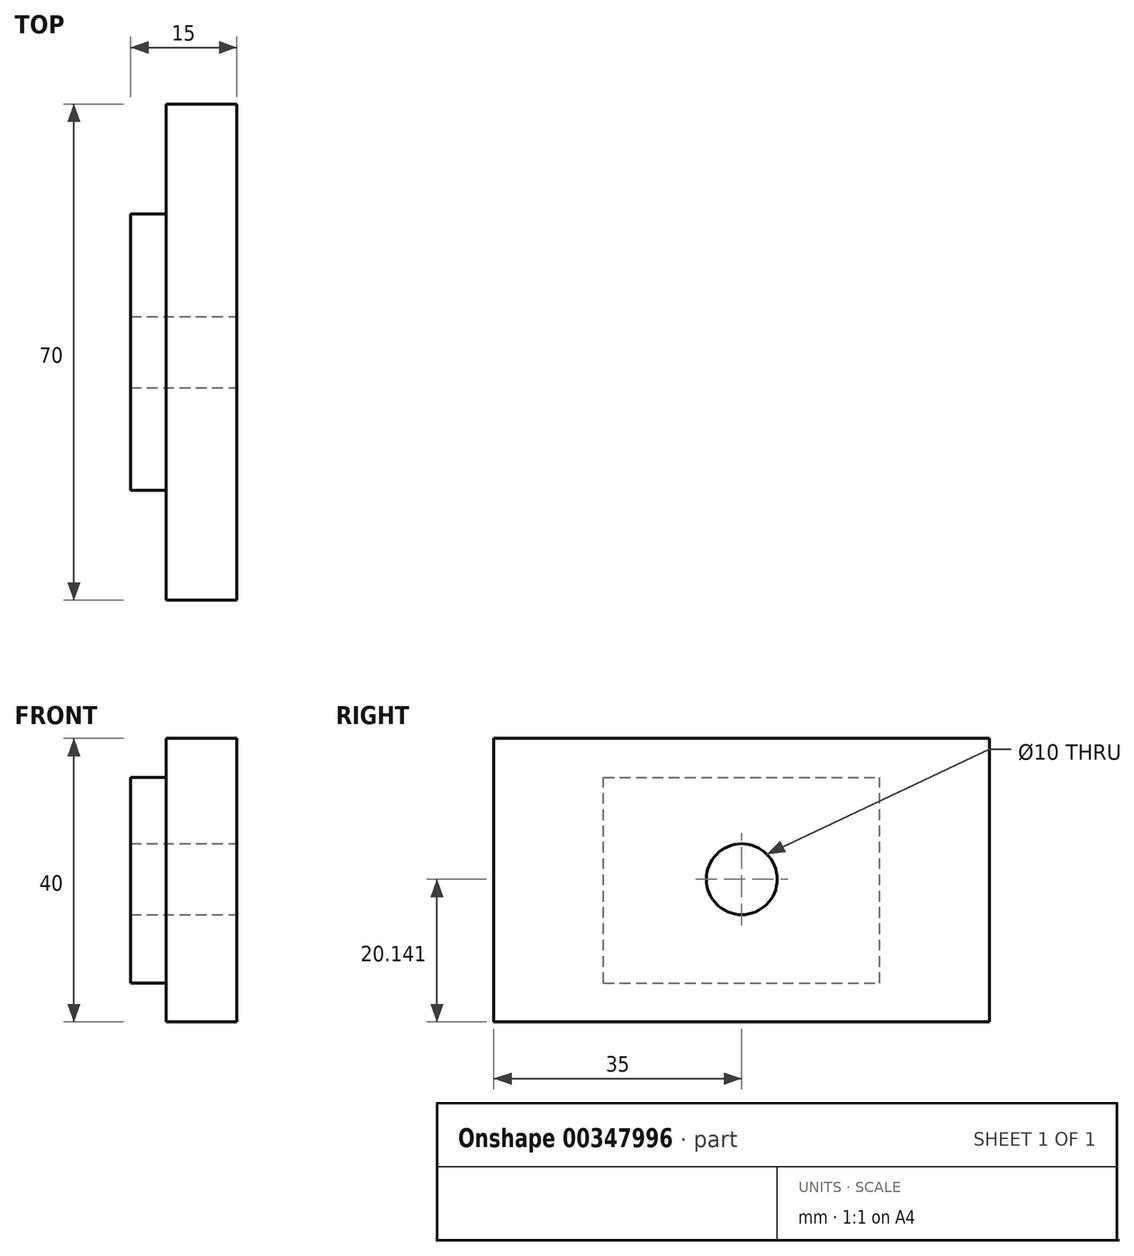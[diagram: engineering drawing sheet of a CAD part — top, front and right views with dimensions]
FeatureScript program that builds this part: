
annotation { "Feature Type Name" : "Feature", "Feature Type Description" : "" }
export const myFeature = defineFeature(function(context is Context, id is Id, definition is map)
    precondition{}
    {
        {
            var Q0;
            Q0=qCreatedBy(makeId("Right.planeOp"),FACE);
            var sketch = newSketch(context, id + "F0", { "sketchPlane" : qUnion([Q0])});
            skLineSegment(sketch, "E0.bottom", {"start": v(0, 0) * mm, "end": v(70, 0) * mm});
            skLineSegment(sketch, "E0.top", {"start": v(0, 40) * mm, "end": v(70, 40) * mm});
            skLineSegment(sketch, "E0.left", {"start": v(0, 0) * mm, "end": v(0, 40) * mm});
            skLineSegment(sketch, "E0.right", {"start": v(70, 0) * mm, "end": v(70, 40) * mm});
            skSolve(sketch);
        }
        {
            var Q0;
            Q0=qSketchRegion(id+"F0",true);
            extrude(context, id + "F1", {"entities" : qUnion([Q0]), "depth" : 10 * mm});
        }
        {
            var Q0;
            Q0=makeQuery(id+"F1.opExtrude","CAP_FACE",FACE,{"disambiguationData":[OSD([sQuery(id+"F0.wireOp",EDGE,"E0.bottom"),sQuery(id+"F0.wireOp",EDGE,"E0.top"),sQuery(id+"F0.wireOp",EDGE,"E0.left"),sQuery(id+"F0.wireOp",EDGE,"E0.right")])],"isStart":false});
            var sketch = newSketch(context, id + "F2", { "sketchPlane" : qUnion([Q0])});
            skLineSegment(sketch, "E1.bottom", {"start": v(15.5, 5.5) * mm, "end": v(54.5, 5.5) * mm});
            skLineSegment(sketch, "E1.top", {"start": v(15.5, 34.5) * mm, "end": v(54.5, 34.5) * mm});
            skLineSegment(sketch, "E1.left", {"start": v(15.5, 5.5) * mm, "end": v(15.5, 34.5) * mm});
            skLineSegment(sketch, "E1.right", {"start": v(54.5, 5.5) * mm, "end": v(54.5, 34.5) * mm});
            skSolve(sketch);
        }
        {
            var Q0;
            Q0=qSketchRegion(id+"F2",true);
            extrude(context, id + "F3", {"entities" : qUnion([Q0]), "operationType" : NewBodyOperationType.ADD, "oppositeDirection" : true, "depth" : 15 * mm});
        }
        {
            var Q0;
            Q0=makeQuery(id+"F1.opExtrude","CAP_FACE",FACE,{"disambiguationData":[OSD([sQuery(id+"F0.wireOp",EDGE,"E0.bottom"),sQuery(id+"F0.wireOp",EDGE,"E0.top"),sQuery(id+"F0.wireOp",EDGE,"E0.left"),sQuery(id+"F0.wireOp",EDGE,"E0.right")])],"isStart":false});
            var sketch = newSketch(context, id + "F4", { "sketchPlane" : qUnion([Q0])});
            skCircle(sketch, "E2", {"center": v(35, 20.14) * mm, "radius": 5 * mm});
            skSolve(sketch);
        }
        {
            var Q0;
            Q0 = qSketchRegion(id + "F4", true);
            extrude(context, id + "F5", {"entities" : qUnion([Q0]), "operationType" : NewBodyOperationType.REMOVE, "oppositeDirection" : true, "depth" : 25 * mm});
        }
    });
